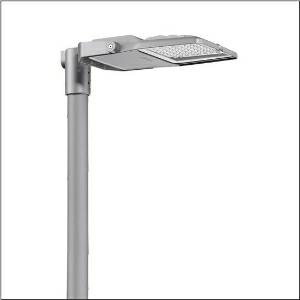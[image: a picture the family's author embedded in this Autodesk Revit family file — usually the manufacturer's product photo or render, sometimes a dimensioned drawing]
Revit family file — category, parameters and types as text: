
# Revit family: floodlight_fl_21_iq_mini___pl61_5xa7772b4c3a_beff
name_source: partatom
category: Lighting Fixtures
units: mm (PartAtom-declared; Revit-internal decimal feet)

## family parameters
Cut with Voids When Loaded = No
Host = Face
Light Source = No
Part Type = Normal
Room Calculation Point = No
Round Connector Dimension = Use Diameter
Shared = No

## types (1)
- --- (1 x LED, 6370 lm, 45.5 W, 4000K)
    Apparent Load = 46 VA
    CIE Flux Codes = 33 65 98 100 100
    Color Rendering = 70
    Color Temperature = 4000K
    Default Elevation = 1800 mm
    Description = Floodlight FL 21 iQ mini, floodlight, primary light control with lens, of PMMA, primary optical cover: protective disc, of toughened safety glass, transparent, light distribution: PL61, light emission: direct distribution, installation type: surface-mounted, LED, High Power LED, rated luminous flux: 6.370lm, luminous efficacy: 140lm/W, light colour: 740, colour temperature: 4000K, control gear: iQ Street-Remote/DALI, control: Auto-Match, Temp-Guard, Night-Set, Smart-Wire, Desk-Remote (wireless, voltage-free reading and setting of iQ features in the workshop via application-optimized NFC function/RFID function), optimised constant luminous flux control (CLO 2.0), Light-Fading, Lumen-Switch, with terminal, 6-pole, mains connection: 220..240V, AC, 50/60Hz, start of lifetime: 46W, end of service life: 48W, reduction: 22W, luminaire housing, of diecast aluminium, powder-coated, Siteco® metallic grey (DB 702S), corrosivity category C5 mid according to DIN EN ISO 12944, suitable for swimming pools, chlorine-resistant, sealing non-destructively replaceable, please order mast flange separately, mast bracket, of steel, galvanised, powder-coated, protection rating (complete): IP66, insulation class (complete): insulation class II (safety insulation), certification: CE, ENEC, VDE, protection symbol: D, impact resistance: IK08, permissible operating ambient temperature: -40..+40°C, permissible operating ambient temperature for outdoor applications: -40..+50°C, standard: DIN EN 12944, LABS conformity tested according to VDMA 24364:2018-05, packaging unit: 1 piece

Light Distribution: PL61
    Height = 70 mm
    Lamp = 1 x LED
    Lamp Light Flux = 6370 lm
    Lamp Power = 45.5 W
    Lamp count = 1
    Length = 485 mm
    Luminous efficacy = 140 lm/W
    Manufacturer = Siteco
    ModVariant = No
    Model = 5XA7772B4C3A
    Number of Poles = 1
    OnlyDefault = Yes
    Power Factor = 1
    Product Name = Floodlight FL 21 iQ mini | PL61
    Product group = floodlight | pylon annexe
    ProductGroupID = 6200
    Protection Class = Protection class II
    Protection Degree = IP 66
    RLX_Detail_Level = 1
    RLX_Emergency_Light_Flux = 0 lm
    RLX_Emergency_Type = 0
    RLX_Emergency_Type_DB = No
    RlxData = <blob elided: 101337 chars, md5=f097eabd>
    Socket = socket
    Standby Power = 0 W
    System Light Flux = 6370 lm
    System Power = 46 W
    Type Comments = factory setting: luminous flux: 100 % | dim-lin: 254 | 463 mA
    Type Image = l_1007125.jpg
    URL = http://relux.com
    VarID = @adj_173440
    Voltage = 0 V
    Weight = 0.00 kg
    Width = 337 mm

## geometry (parser evidence)
native form markers: Blend x4, Sweep x10
no freeform markers — native parametric forms only
